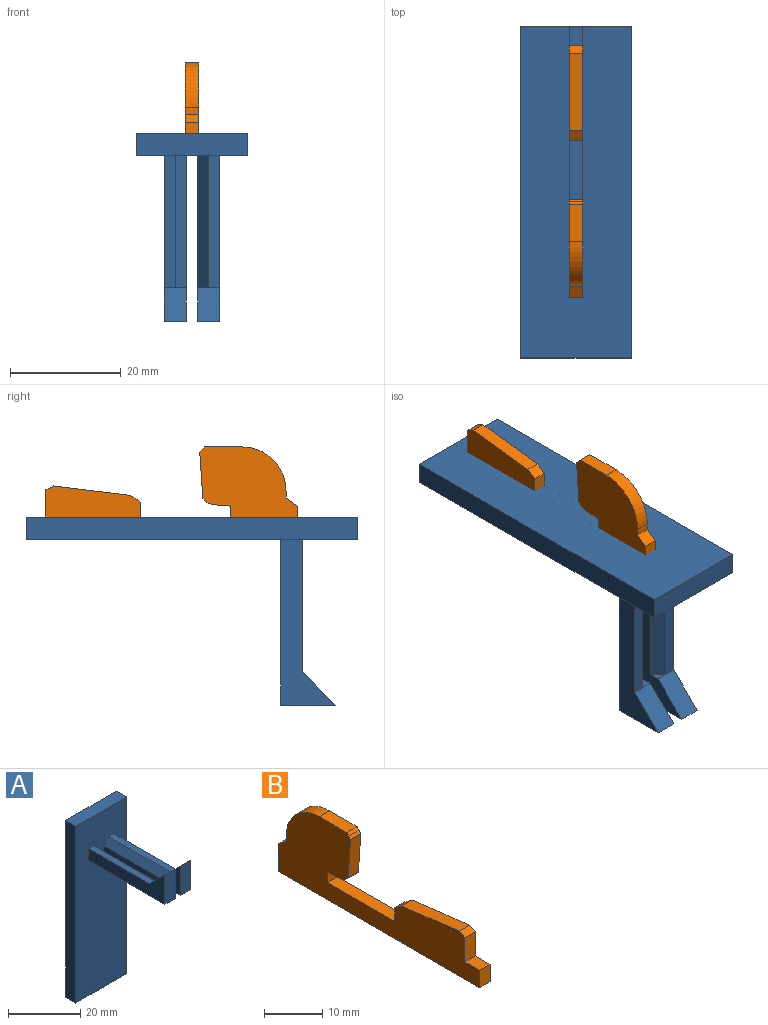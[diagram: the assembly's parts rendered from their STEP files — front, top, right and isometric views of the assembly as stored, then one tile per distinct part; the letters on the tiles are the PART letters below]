
ASSEMBLY  parts=2 mates=1
PART A: 22 faces, bbox 20x34x60 mm
  f0: plane 24x2mm, normal (0,0,1), area 48mm2, adj f2,f14,f18,f20
  f1: plane 24x2mm, normal (0,0,1), area 48mm2, adj f2,f8,f19,f21
  f2: plane 60x20mm, normal (0,-1,0), area 1172mm2, adj f0,f1,f3,f4,f5,f6,f8,f9
  f3: plane 20x4mm, normal (0,0,-1), area 80mm2, adj f2,f4,f6,f7
  f4: plane 60x4mm, normal (1,0,0), area 240mm2, adj f2,f3,f5,f7
  f5: plane 20x4mm, normal (0,0,1), area 80mm2, adj f2,f4,f6,f7
  f6: plane 60x4mm, normal (-1,0,0), area 240mm2, adj f2,f3,f5,f7
  f7: plane 60x20mm, normal (0,1,0), area 1200mm2, adj f3,f4,f5,f6
  f8: plane 30x10mm, normal (-1,0,0), area 138mm2, adj f1,f2,f9,f11,f21
  f9: plane 30x4mm, normal (0,0,-1), area 120mm2, adj f2,f8,f10,f11
  f10: plane 30x10mm, normal (1,0,0), area 90mm2, adj f2,f9,f11,f16,f19,f21
  f11: plane 10x4mm, normal (0,-1,0), area 40mm2, adj f8,f9,f10,f21
  f12: plane 30x10mm, normal (-1,0,0), area 90mm2, adj f2,f13,f15,f17,f18,f20
  f13: plane 30x4mm, normal (0,0,-1), area 120mm2, adj f2,f12,f14,f15
  f14: plane 30x10mm, normal (1,0,0), area 138mm2, adj f0,f2,f13,f15,f20
  f15: plane 10x4mm, normal (0,-1,0), area 40mm2, adj f12,f13,f14,f20
  f16: plane 2x2mm, normal (0,1,0), area 2mm2, adj f10,f19,f21
  f17: plane 2x2mm, normal (0,1,0), area 2mm2, adj f12,f18,f20
  f18: plane 24x2mm, normal (-0.71,0,0.71), area 67.9mm2, adj f0,f2,f12,f17
  f19: plane 24x2mm, normal (0.71,0,0.71), area 67.9mm2, adj f1,f2,f10,f16
  f20: plane 6x6mm, normal (0,0.71,0.71), area 33.9mm2, adj f0,f12,f14,f15,f17
  f21: plane 6x6mm, normal (0,0.71,0.71), area 33.9mm2, adj f1,f8,f10,f11,f16
PART B: 24 faces, bbox 2.5x49x16.5 mm
  f0: plane 6.71x2.5mm, normal (0,0,1), area 16.8mm2, adj f4,f5,f8,f10
  f1: plane 49x2.5mm, normal (0,0,-1), area 122.5mm2, adj f2,f3,f4,f5
  f2: plane 5.77x2.5mm, normal (0,1,0), area 14.4mm2, adj f1,f4,f5,f7
  f3: plane 3.65x2.5mm, normal (0,-1,0), area 9.1mm2, adj f1,f4,f5,f11
  f4: plane 49x16.5mm, normal (1,0,0), area 436.7mm2, adj f0,f1,f2,f3,f6,f7,f8,f9
  f5: plane 49x16.5mm, normal (-1,0,0), area 436.7mm2, adj f0,f1,f2,f3,f6,f7,f8,f9
  f6: plane 2.5x1.26mm, normal (0,1,0), area 3.2mm2, adj f4,f5,f7,f8
  f7: plane 2.5x2mm, normal (0,0.59,0.81), area 6.2mm2, adj f2,f4,f5,f6
  f8: cylinder r=8mm len=8mm, axis (1,0,0), area 31.4mm2, adj f0,f4,f5,f6
  f9: plane 2.5x0.51mm, normal (0,-0.78,0.63), area 1.6mm2, adj f4,f5,f10,f23
  f10: plane 2.5x0.52mm, normal (0,-0.74,0.68), area 1.8mm2, adj f0,f4,f5,f9
  f11: plane 3.59x2.5mm, normal (0,0,1), area 9mm2, adj f3,f4,f5,f12
  f12: plane 5.1x2.5mm, normal (0,-1,0), area 12.8mm2, adj f4,f5,f11,f13
  f13: plane 2.5x1.37mm, normal (0,-0.45,0.89), area 3.8mm2, adj f4,f5,f12,f14
  f14: plane 13.97x2.5mm, normal (0,0.12,0.99), area 35.2mm2, adj f4,f5,f13,f15
  f15: plane 2.5x1.71mm, normal (0,0.58,0.81), area 5.3mm2, adj f4,f5,f14,f16
  f16: plane 2.85x2.5mm, normal (0,1,0), area 7.1mm2, adj f4,f5,f15,f17
  f17: plane 16.29x2.5mm, normal (0,0,1), area 40.7mm2, adj f4,f5,f16,f18
  f18: plane 2.5x2.14mm, normal (0,-1,0), area 5.4mm2, adj f4,f5,f17,f19
  f19: plane 2.93x2.5mm, normal (0,-0.08,-1), area 7.4mm2, adj f4,f5,f18,f20
  f20: plane 2.5x1.09mm, normal (0,-0.2,-0.98), area 2.8mm2, adj f4,f5,f19,f21
  f21: plane 2.5x0.63mm, normal (0,-0.63,-0.77), area 2mm2, adj f4,f5,f20,f22
  f22: plane 2.5x0.34mm, normal (0,-0.72,-0.69), area 1.2mm2, adj f4,f5,f21,f23
  f23: plane 8.36x2.5mm, normal (0,-1,-0.07), area 20.9mm2, adj f4,f5,f9,f22
PLACE A rot(axis=(1,0,0),90deg) t=(0,0,0)mm
PLACE B rot(axis=(0,0,1),180deg) t=(1.25,3.5,2.67)mm
MATE planar A.f3 <-> B.f3  axis (0,1,0) through (0,30,-2)mm
